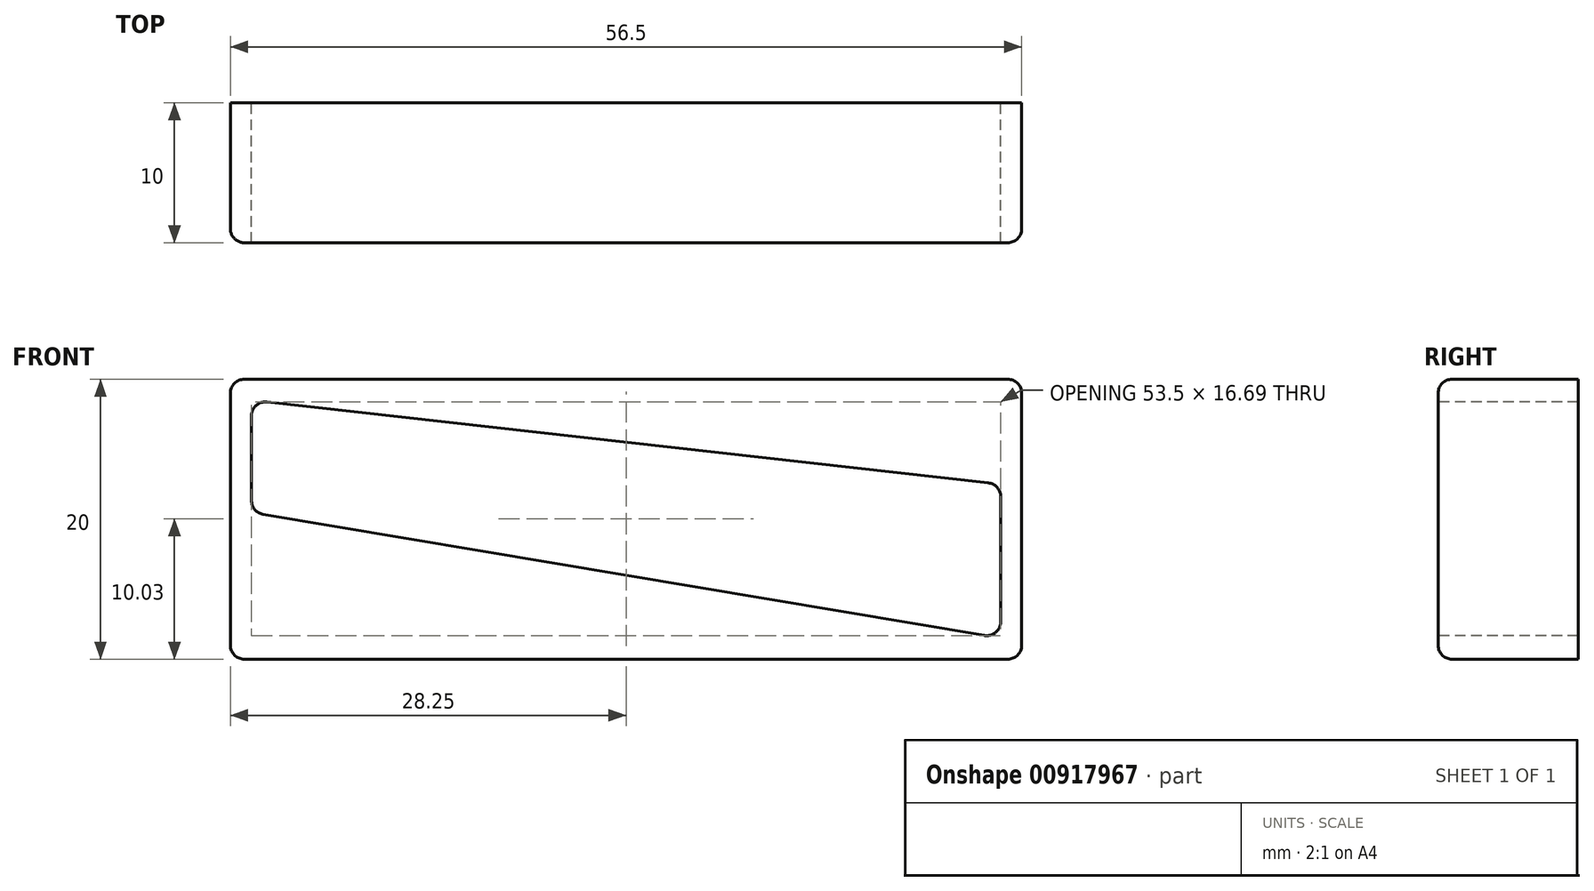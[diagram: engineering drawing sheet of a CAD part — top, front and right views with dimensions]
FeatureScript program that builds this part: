
annotation { "Feature Type Name" : "Feature", "Feature Type Description" : "" }
export const myFeature = defineFeature(function(context is Context, id is Id, definition is map)
    precondition{}
    {
        {
            var Q0;
            Q0=qCreatedBy(makeId("Front.planeOp"),FACE);
            var sketch = newSketch(context, id + "F0", { "sketchPlane" : qUnion([Q0])});
            skLineSegment(sketch, "E0", {"start": v(0, 0) * mm, "end": v(53.5, 0) * mm});
            skLineSegment(sketch, "E1", {"start": v(0, 0) * mm, "end": v(0, 9) * mm});
            skLineSegment(sketch, "E2", {"start": v(0, 9) * mm, "end": v(0, 17) * mm});
            skLineSegment(sketch, "E3", {"start": v(53.5, 0) * mm, "end": v(53.5, 11) * mm});
            skLineSegment(sketch, "E4", {"start": v(0, 17) * mm, "end": v(53.5, 11) * mm});
            skLineSegment(sketch, "E5", {"start": v(0, 9) * mm, "end": v(53.5, 0) * mm});
            skLineSegment(sketch, "E6", {"start": v(0, 0) * mm, "end": v(0, -1.5) * mm});
            skLineSegment(sketch, "E7", {"start": v(0, 0) * mm, "end": v(-1.5, 0) * mm});
            skLineSegment(sketch, "E8", {"start": v(-1.5, 0) * mm, "end": v(-1.5, -1.5) * mm});
            skLineSegment(sketch, "E9", {"start": v(-1.5, -1.5) * mm, "end": v(55, -1.5) * mm});
            skLineSegment(sketch, "E10", {"start": v(55, -1.5) * mm, "end": v(55, 18.5) * mm});
            skLineSegment(sketch, "E11", {"start": v(55, 18.5) * mm, "end": v(-1.5, 18.5) * mm});
            skLineSegment(sketch, "E12", {"start": v(-1.5, 18.5) * mm, "end": v(-1.5, 0) * mm});
            skLineSegment(sketch, "E13", {"start": v(53.5, 11) * mm, "end": v(53.5, 18.5) * mm});
            skLineSegment(sketch, "E14", {"start": v(53.5, 0) * mm, "end": v(53.5, -1.5) * mm});
            skSolve(sketch);
        }
        {
            var Q0;
            Q0=makeQuery(id+"F0.imprint","IMPRINT",FACE,{"disambiguationData":[TD([[makeQuery(id+"F0.imprint","IMPRINT",EDGE,{"derivedFrom":sQuery(id+"F0.wireOp",EDGE,"E0")}),-1.0]])]});
            var Q1;
            Q1=makeQuery(id+"F0.imprint","IMPRINT",FACE,{"disambiguationData":[TD([[makeQuery(id+"F0.imprint","IMPRINT",EDGE,{"derivedFrom":sQuery(id+"F0.wireOp",EDGE,"E0")}),1.0]])]});
            var Q2;
            {var subQ0=sQuery(id+"F0.wireOp",EDGE,"E6");Q2=makeQuery(id+"F0.imprint","IMPRINT",FACE,{"disambiguationData":[TD([[makeQuery(id+"F0.imprint","IMPRINT",EDGE,{"derivedFrom":subQ0}),-1.0]])]});}
            var Q3;
            Q3=makeQuery(id+"F0.imprint","IMPRINT",FACE,{"disambiguationData":[TD([[makeQuery(id+"F0.imprint","IMPRINT",EDGE,{"derivedFrom":sQuery(id+"F0.wireOp",EDGE,"E3")}),-1.0]])]});
            var Q4;
            Q4=makeQuery(id+"F0.imprint","IMPRINT",FACE,{"disambiguationData":[TD([[makeQuery(id+"F0.imprint","IMPRINT",EDGE,{"derivedFrom":sQuery(id+"F0.wireOp",EDGE,"E1")}),1.0]])]});
            extrude(context, id + "F1", {"entities" : qUnion([Q0, Q1, Q2, Q3, Q4]), "depth" : 10 * mm, "offsetDistance" : 25 * mm});
        }
        {
            var Q0;
            Q0=makeQuery(id+"F1.opExtrude","CAP_EDGE",EDGE,{"disambiguationData":[OSD([sQuery(id+"F0.wireOp",EDGE,"E10")])],"isStart":false});
            var Q1;
            Q1=makeQuery(id+"F1.opExtrude","CAP_EDGE",EDGE,{"disambiguationData":[OSD([sQuery(id+"F0.wireOp",EDGE,"E11")])],"isStart":false});
            var Q2;
            Q2=makeQuery(id+"F1.opExtrude","CAP_EDGE",EDGE,{"disambiguationData":[OSD([sQuery(id+"F0.wireOp",EDGE,"E9")])],"isStart":false});
            var Q3;
            Q3=makeQuery(id+"F1.opExtrude","CAP_EDGE",EDGE,{"disambiguationData":[OSD([sQuery(id+"F0.wireOp",EDGE,"E12")])],"isStart":false});
            var Q4;
            Q4=makeQuery(id+"F1.opExtrude","CAP_EDGE",EDGE,{"disambiguationData":[OSD([sQuery(id+"F0.wireOp",EDGE,"E8")])],"isStart":false});
            var Q5;
            Q5=makeQuery(id+"F1.opExtrude","SWEPT_EDGE",EDGE,{"disambiguationData":[OSD([sQuery(id+"F0.wireOp",EDGE,"E8"),sQuery(id+"F0.wireOp",EDGE,"E9")])]});
            var Q6;
            Q6=makeQuery(id+"F1.opExtrude","SWEPT_EDGE",EDGE,{"disambiguationData":[OSD([sQuery(id+"F0.wireOp",EDGE,"E11"),sQuery(id+"F0.wireOp",EDGE,"E12")])]});
            var Q7;
            Q7=makeQuery(id+"F1.opExtrude","SWEPT_EDGE",EDGE,{"disambiguationData":[OSD([sQuery(id+"F0.wireOp",EDGE,"E10"),sQuery(id+"F0.wireOp",EDGE,"E11")])]});
            var Q8;
            Q8=makeQuery(id+"F1.opExtrude","SWEPT_EDGE",EDGE,{"disambiguationData":[OSD([sQuery(id+"F0.wireOp",EDGE,"E9"),sQuery(id+"F0.wireOp",EDGE,"E10")])]});
            fillet(context, id + "F2", {"entities" : qUnion([Q0, Q1, Q2, Q3, Q4, Q5, Q6, Q7, Q8]), "radius" : 1 * mm, "tangentPropagation" : true, "allowEdgeOverflow" : false});
        }
        {
            var Q0;
            Q0=makeQuery(id+"F1.opExtrude","SWEPT_EDGE",EDGE,{"disambiguationData":[OSD([sQuery(id+"F0.wireOp",EDGE,"E2"),sQuery(id+"F0.wireOp",EDGE,"E4")])]});
            var Q1;
            Q1=makeQuery(id+"F1.opExtrude","SWEPT_EDGE",EDGE,{"disambiguationData":[OSD([sQuery(id+"F0.wireOp",EDGE,"E1"),sQuery(id+"F0.wireOp",EDGE,"E2"),sQuery(id+"F0.wireOp",EDGE,"E5")])]});
            var Q2;
            Q2=makeQuery(id+"F1.opExtrude","SWEPT_EDGE",EDGE,{"disambiguationData":[OSD([sQuery(id+"F0.wireOp",EDGE,"E3"),sQuery(id+"F0.wireOp",EDGE,"E4"),sQuery(id+"F0.wireOp",EDGE,"E13")])]});
            var Q3;
            Q3=makeQuery(id+"F1.opExtrude","SWEPT_EDGE",EDGE,{"disambiguationData":[OSD([sQuery(id+"F0.wireOp",EDGE,"E0"),sQuery(id+"F0.wireOp",EDGE,"E3"),sQuery(id+"F0.wireOp",EDGE,"E5"),sQuery(id+"F0.wireOp",EDGE,"E14")])]});
            fillet(context, id + "F3", {"entities" : qUnion([Q0, Q1, Q2, Q3]), "radius" : 1 * mm, "tangentPropagation" : true, "allowEdgeOverflow" : false});
        }
    });
